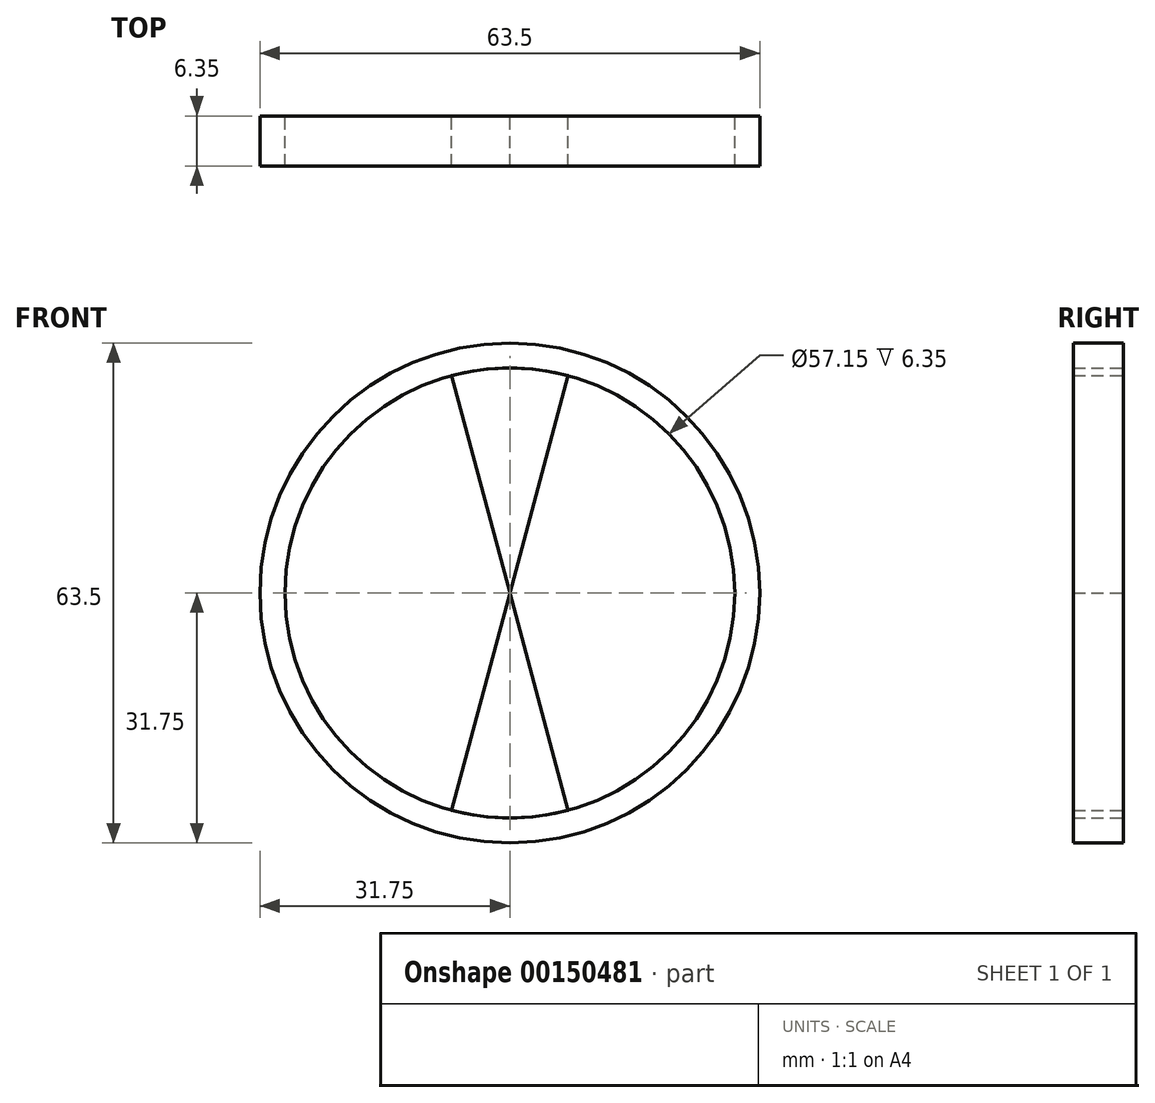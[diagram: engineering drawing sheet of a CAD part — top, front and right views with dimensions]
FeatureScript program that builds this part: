
annotation { "Feature Type Name" : "Feature", "Feature Type Description" : "" }
export const myFeature = defineFeature(function(context is Context, id is Id, definition is map)
    precondition{}
    {
        {
            var Q0;
            Q0=qCreatedBy(makeId("Front.planeOp"),FACE);
            var sketch = newSketch(context, id + "F0", { "sketchPlane" : qUnion([Q0])});
            skCircle(sketch, "E0", {"center": v(0, 0) * mm, "radius": 31.75 * mm});
            skCircle(sketch, "E1", {"center": v(0, 0) * mm, "radius": 28.58 * mm});
            skLineSegment(sketch, "E2", {"start": v(0, 0) * mm, "end": v(-27.6, 7.4) * mm});
            skLineSegment(sketch, "E3", {"start": v(0, 0) * mm, "end": v(-27.6, -7.4) * mm});
            skLineSegment(sketch, "E4", {"start": v(0, 0) * mm, "end": v(27.6, 7.4) * mm});
            skLineSegment(sketch, "E5", {"start": v(0, 0) * mm, "end": v(27.6, -7.4) * mm});
            skLineSegment(sketch, "E6", {"start": v(0, 0) * mm, "end": v(-7.4, 27.6) * mm});
            skLineSegment(sketch, "E7", {"start": v(0, 0) * mm, "end": v(7.4, 27.6) * mm});
            skLineSegment(sketch, "E8", {"start": v(0, 0) * mm, "end": v(-7.4, -27.6) * mm});
            skLineSegment(sketch, "E9", {"start": v(0, 0) * mm, "end": v(7.4, -27.6) * mm});
            skSolve(sketch);
        }
        {
            var Q0;
            Q0=makeQuery(id+"F0.imprint","IMPRINT",FACE,{"disambiguationData":[TD([[makeQuery(id+"F0.imprint","IMPRINT",EDGE,{"derivedFrom":sQuery(id+"F0.wireOp",EDGE,"E0")}),1.0]])]});
            extrude(context, id + "F1", {"entities" : qUnion([Q0]), "depth" : 6.35 * mm});
        }
        {
            var Q0;
            Q0=qCreatedBy(makeId("Front.planeOp"),FACE);
            var sketch = newSketch(context, id + "F2", { "sketchPlane" : qUnion([Q0])});
            skLineSegment(sketch, "E10", {"start": v(0, 0) * mm, "end": v(-7.4, 27.6) * mm});
            skLineSegment(sketch, "E11", {"start": v(0, 0) * mm, "end": v(7.4, 27.6) * mm});
            skLineSegment(sketch, "E12.MirrorCS", {"start": v(0, 0) * mm, "end": v(7.4, -27.6) * mm});
            skLineSegment(sketch, "E13.MirrorCS", {"start": v(0, 0) * mm, "end": v(-7.4, -27.6) * mm});
            skArc(sketch, "E14", {"start": v(7.4, 27.6) * mm, "mid": v(0, 28.58) * mm, "end": v(-7.4, 27.6) * mm});
            skArc(sketch, "E15.MirrorCS", {"start": v(7.4, -27.6) * mm, "mid": v(0, -28.58) * mm, "end": v(-7.4, -27.6) * mm});
            skSolve(sketch);
        }
        {
            var Q0;
            Q0 = qSketchRegion(id + "F2", true);
            extrude(context, id + "F3", {"entities" : qUnion([Q0]), "depth" : 6.35 * mm});
        }
    });
